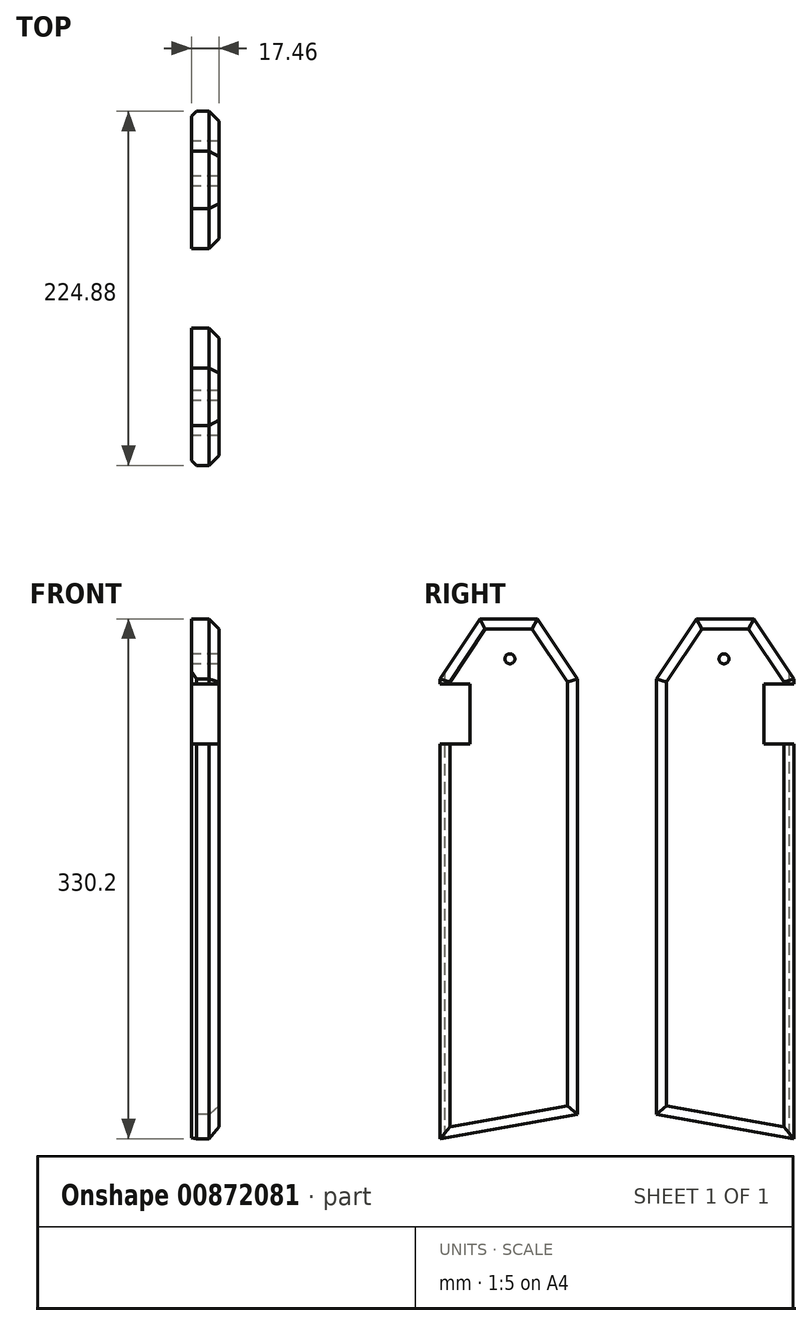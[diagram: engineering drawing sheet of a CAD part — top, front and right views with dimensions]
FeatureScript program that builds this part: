
annotation { "Feature Type Name" : "Feature", "Feature Type Description" : "" }
export const myFeature = defineFeature(function(context is Context, id is Id, definition is map)
    precondition{}
    {
        {
            var Q0;
            Q0=qCreatedBy(makeId("Right.planeOp"),FACE);
            var sketch = newSketch(context, id + "F0", { "sketchPlane" : qUnion([Q0])});
            skLineSegment(sketch, "E0.bottom", {"start": v(0, 0) * mm, "end": v(-87.31, 0) * mm, "construction": true});
            skLineSegment(sketch, "E0.top", {"start": v(0, -330.2) * mm, "end": v(-87.31, -330.2) * mm, "construction": true});
            skLineSegment(sketch, "E0.left", {"start": v(0, -38.1) * mm, "end": v(0, -314.8) * mm});
            skLineSegment(sketch, "E0.right", {"start": v(-87.31, -38.1) * mm, "end": v(-87.31, -41.27) * mm});
            skLineSegment(sketch, "E1", {"start": v(-87.31, -330.2) * mm, "end": v(0, -314.8) * mm});
            skLineSegment(sketch, "E2", {"start": v(0, -330.2) * mm, "end": v(0, -314.8) * mm, "construction": true});
            skCircle(sketch, "E3", {"center": v(-42.86, -25.4) * mm, "radius": 3.18 * mm});
            skLineSegment(sketch, "E4", {"start": v(-87.31, -38.1) * mm, "end": v(-61.91, 0) * mm});
            skLineSegment(sketch, "E5", {"start": v(-61.91, 0) * mm, "end": v(-25.4, 0) * mm});
            skLineSegment(sketch, "E6", {"start": v(-25.4, 0) * mm, "end": v(0, -38.1) * mm});
            skLineSegment(sketch, "E7", {"start": v(-87.31, -38.1) * mm, "end": v(-87.31, 0) * mm, "construction": true});
            skLineSegment(sketch, "E8", {"start": v(0, 0) * mm, "end": v(0, -38.1) * mm, "construction": true});
            skLineSegment(sketch, "E9", {"start": v(25.13, 0) * mm, "end": v(25.13, -330.2) * mm, "construction": true});
            skCircle(sketch, "E10.MirrorC", {"center": v(93.12, -25.4) * mm, "radius": 3.18 * mm});
            skLineSegment(sketch, "E11.MirrorCS", {"start": v(112.17, 0) * mm, "end": v(75.66, 0) * mm});
            skLineSegment(sketch, "E12.MirrorCS", {"start": v(50.26, -38.1) * mm, "end": v(50.26, -314.8) * mm});
            skLineSegment(sketch, "E13.MirrorCS", {"start": v(137.57, -330.2) * mm, "end": v(50.26, -314.8) * mm});
            skLineSegment(sketch, "E14.MirrorCS", {"start": v(50.26, -330.2) * mm, "end": v(50.26, -314.8) * mm, "construction": true});
            skLineSegment(sketch, "E15.MirrorCS", {"start": v(137.57, -38.1) * mm, "end": v(112.17, 0) * mm});
            skLineSegment(sketch, "E16.MirrorCS", {"start": v(75.66, 0) * mm, "end": v(50.26, -38.1) * mm});
            skLineSegment(sketch, "E17.MirrorCS", {"start": v(137.57, -38.1) * mm, "end": v(137.57, 0) * mm, "construction": true});
            skLineSegment(sketch, "E18.MirrorCS", {"start": v(50.26, 0) * mm, "end": v(50.26, -38.1) * mm, "construction": true});
            skLineSegment(sketch, "E19.MirrorCS", {"start": v(50.26, 0) * mm, "end": v(137.57, 0) * mm, "construction": true});
            skLineSegment(sketch, "E20.MirrorCS", {"start": v(50.26, -330.2) * mm, "end": v(137.57, -330.2) * mm, "construction": true});
            skLineSegment(sketch, "E21.MirrorCS", {"start": v(50.26, -38.1) * mm, "end": v(137.57, -38.1) * mm, "construction": true});
            skLineSegment(sketch, "E22", {"start": v(-87.31, -38.1) * mm, "end": v(0, -38.1) * mm, "construction": true});
            skLineSegment(sketch, "E23", {"start": v(-87.31, -41.27) * mm, "end": v(-68.26, -41.27) * mm});
            skLineSegment(sketch, "E24", {"start": v(-68.26, -41.27) * mm, "end": v(-68.26, -79.37) * mm});
            skLineSegment(sketch, "E25", {"start": v(-68.26, -79.37) * mm, "end": v(-87.31, -79.37) * mm});
            skLineSegment(sketch, "E26.trimOffspring", {"start": v(-87.31, -79.37) * mm, "end": v(-87.31, -330.2) * mm});
            skLineSegment(sketch, "E27.MirrorCS", {"start": v(137.57, -41.27) * mm, "end": v(118.52, -41.27) * mm});
            skLineSegment(sketch, "E28.MirrorCS", {"start": v(118.52, -41.27) * mm, "end": v(118.52, -79.37) * mm});
            skLineSegment(sketch, "E29.MirrorCS", {"start": v(118.52, -79.37) * mm, "end": v(137.57, -79.37) * mm});
            skLineSegment(sketch, "E30.MirrorCS", {"start": v(137.57, -38.1) * mm, "end": v(137.57, -41.27) * mm});
            skLineSegment(sketch, "E31.MirrorCS", {"start": v(137.57, -79.37) * mm, "end": v(137.57, -330.2) * mm});
            skSolve(sketch);
        }
        {
            var Q0;
            Q0=qSketchRegion(id+"F0",true);
            extrude(context, id + "F1", {"entities" : qUnion([Q0]), "depth" : 17.46 * mm});
        }
        {
            var Q0;
            Q0=makeQuery(id+"F1.opExtrude","CAP_EDGE",EDGE,{"disambiguationData":[OSD([sQuery(id+"F0.wireOp",EDGE,"E4")])],"isStart":false});
            var Q1;
            Q1=makeQuery(id+"F1.opExtrude","CAP_EDGE",EDGE,{"disambiguationData":[OSD([sQuery(id+"F0.wireOp",EDGE,"E5")])],"isStart":false});
            var Q2;
            Q2=makeQuery(id+"F1.opExtrude","CAP_EDGE",EDGE,{"disambiguationData":[OSD([sQuery(id+"F0.wireOp",EDGE,"E6")])],"isStart":false});
            var Q3;
            Q3=makeQuery(id+"F1.opExtrude","CAP_EDGE",EDGE,{"disambiguationData":[OSD([sQuery(id+"F0.wireOp",EDGE,"E0.left")])],"isStart":false});
            var Q4;
            Q4=makeQuery(id+"F1.opExtrude","CAP_EDGE",EDGE,{"disambiguationData":[OSD([sQuery(id+"F0.wireOp",EDGE,"E0.right")])],"isStart":false});
            var Q5;
            Q5=makeQuery(id+"F1.opExtrude","CAP_EDGE",EDGE,{"disambiguationData":[OSD([sQuery(id+"F0.wireOp",EDGE,"E1")])],"isStart":false});
            var Q6;
            Q6=makeQuery(id+"F1.opExtrude","CAP_EDGE",EDGE,{"disambiguationData":[OSD([sQuery(id+"F0.wireOp",EDGE,"E13.MirrorCS")])],"isStart":false});
            var Q7;
            Q7=makeQuery(id+"F1.opExtrude","CAP_EDGE",EDGE,{"disambiguationData":[OSD([sQuery(id+"F0.wireOp",EDGE,"E12.MirrorCS")])],"isStart":false});
            var Q8;
            Q8=makeQuery(id+"F1.opExtrude","CAP_EDGE",EDGE,{"disambiguationData":[OSD([sQuery(id+"F0.wireOp",EDGE,"f23bf8ea-3d05-4a58-b799-b011d6196e993.MirrorCS")])],"isStart":false});
            var Q9;
            Q9=makeQuery(id+"F1.opExtrude","CAP_EDGE",EDGE,{"disambiguationData":[OSD([sQuery(id+"F0.wireOp",EDGE,"E15.MirrorCS")])],"isStart":false});
            var Q10;
            Q10=makeQuery(id+"F1.opExtrude","CAP_EDGE",EDGE,{"disambiguationData":[OSD([sQuery(id+"F0.wireOp",EDGE,"E11.MirrorCS")])],"isStart":false});
            var Q11;
            Q11=makeQuery(id+"F1.opExtrude","CAP_EDGE",EDGE,{"disambiguationData":[OSD([sQuery(id+"F0.wireOp",EDGE,"E16.MirrorCS")])],"isStart":false});
            var Q12;
            Q12=makeQuery(id+"F1.opExtrude","CAP_EDGE",EDGE,{"disambiguationData":[OSD([sQuery(id+"F0.wireOp",EDGE,"E26.trimOffspring")])],"isStart":false});
            var Q13;
            Q13=makeQuery(id+"F1.opExtrude","CAP_EDGE",EDGE,{"disambiguationData":[OSD([sQuery(id+"F0.wireOp",EDGE,"E31.MirrorCS")])],"isStart":false});
            var Q14;
            Q14=makeQuery(id+"F1.opExtrude","CAP_EDGE",EDGE,{"disambiguationData":[OSD([sQuery(id+"F0.wireOp",EDGE,"E30.MirrorCS")])],"isStart":false});
            chamfer(context, id + "F2", {"entities" : qUnion([Q0, Q1, Q2, Q3, Q4, Q5, Q6, Q7, Q8, Q9, Q10, Q11, Q12, Q13, Q14]), "width" : 6.35 * mm, "tangentPropagation" : true});
        }
        {
            var Q0;
            Q0=makeQuery(id+"F1.opExtrude","CAP_EDGE",EDGE,{"disambiguationData":[OSD([sQuery(id+"F0.wireOp",EDGE,"E31.MirrorCS")])],"isStart":true});
            var Q1;
            Q1=makeQuery(id+"F1.opExtrude","CAP_EDGE",EDGE,{"disambiguationData":[OSD([sQuery(id+"F0.wireOp",EDGE,"E30.MirrorCS")])],"isStart":true});
            var Q2;
            Q2=makeQuery(id+"F1.opExtrude","CAP_EDGE",EDGE,{"disambiguationData":[OSD([sQuery(id+"F0.wireOp",EDGE,"E0.right")])],"isStart":true});
            var Q3;
            Q3=makeQuery(id+"F1.opExtrude","CAP_EDGE",EDGE,{"disambiguationData":[OSD([sQuery(id+"F0.wireOp",EDGE,"E26.trimOffspring")])],"isStart":true});
            chamfer(context, id + "F3", {"entities" : qUnion([Q0, Q1, Q2, Q3]), "width" : 3.17 * mm, "tangentPropagation" : true});
        }
    });
